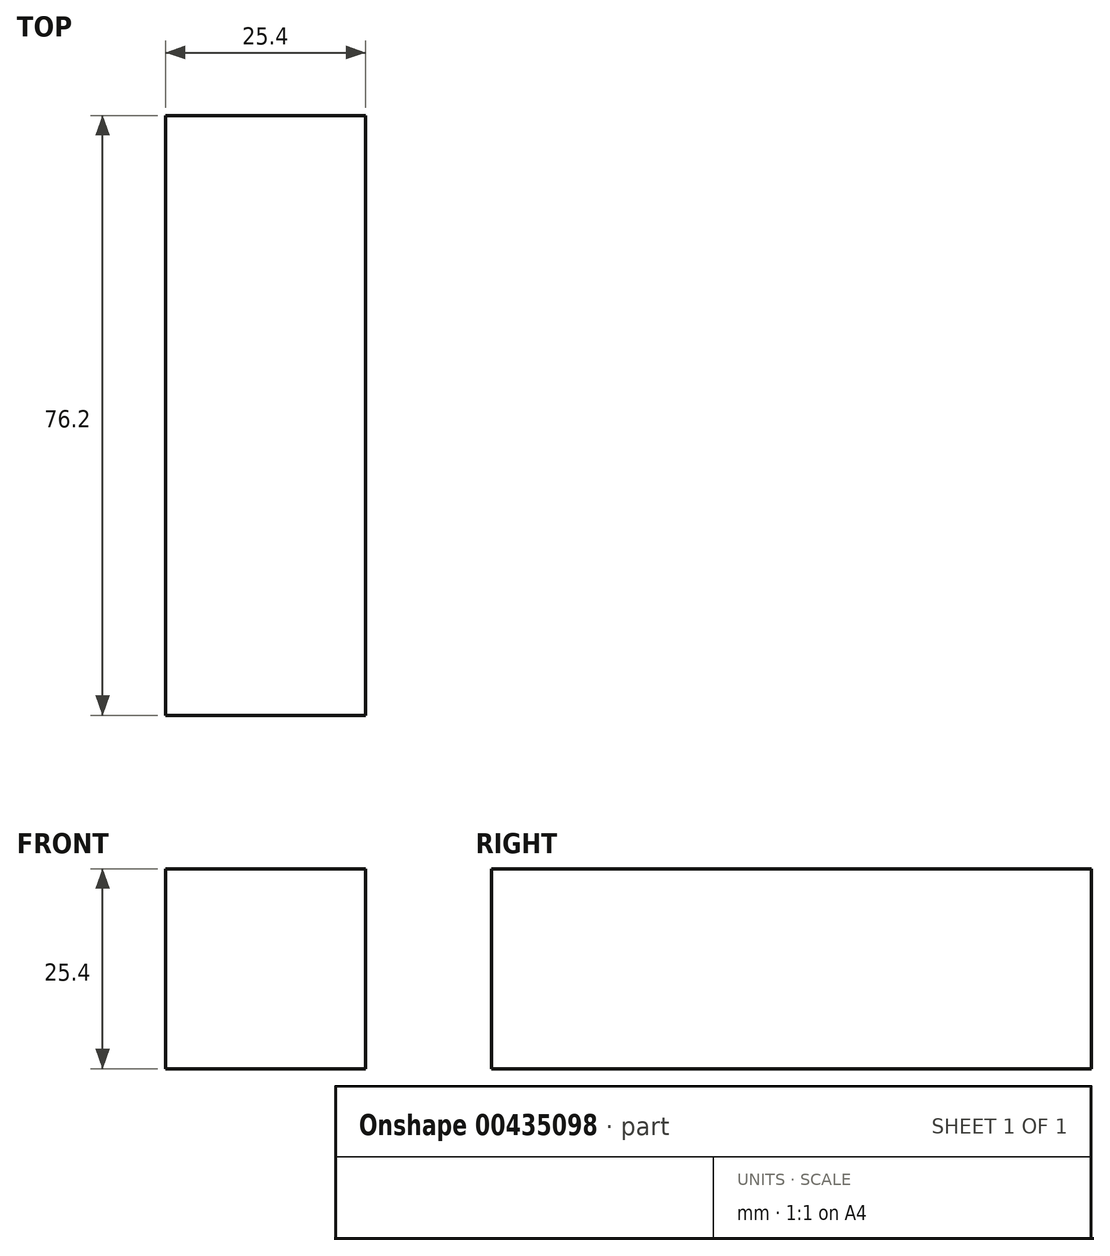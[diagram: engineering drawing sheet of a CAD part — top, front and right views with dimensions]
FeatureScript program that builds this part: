
annotation { "Feature Type Name" : "Feature", "Feature Type Description" : "" }
export const myFeature = defineFeature(function(context is Context, id is Id, definition is map)
    precondition{}
    {
        {
            var Q0;
            Q0=qCreatedBy(makeId("Front.planeOp"),FACE);
            var sketch = newSketch(context, id + "F0", { "sketchPlane" : qUnion([Q0])});
            skLineSegment(sketch, "E0.bottom", {"start": v(16.62, 40.3) * mm, "end": v(-8.78, 40.3) * mm});
            skLineSegment(sketch, "E0.top", {"start": v(16.62, 14.9) * mm, "end": v(-8.78, 14.9) * mm});
            skLineSegment(sketch, "E0.left", {"start": v(16.62, 40.3) * mm, "end": v(16.62, 14.9) * mm});
            skLineSegment(sketch, "E0.right", {"start": v(-8.78, 40.3) * mm, "end": v(-8.78, 14.9) * mm});
            skSolve(sketch);
        }
        {
            var Q0;
            Q0=makeQuery(id+"F0.imprint","IMPRINT",FACE,{"disambiguationData":[TD([[makeQuery(id+"F0.imprint","IMPRINT",EDGE,{"derivedFrom":sQuery(id+"F0.wireOp",EDGE,"E0.bottom")}),1.0]])]});
            var sketch = newSketch(context, id + "F1", { "sketchPlane" : qUnion([Q0])});
            skSolve(sketch);
        }
        {
            var Q0;
            Q0 = qSketchRegion(id + "F1", true);
            var Q1;
            Q1=makeQuery(id+"F0.imprint","IMPRINT",FACE,{"disambiguationData":[TD([[makeQuery(id+"F0.imprint","IMPRINT",EDGE,{"derivedFrom":sQuery(id+"F0.wireOp",EDGE,"E0.bottom")}),1.0]])]});
            extrude(context, id + "F2", {"entities" : qUnion([Q0, Q1]), "depth" : 76.2 * mm});
        }
    });
